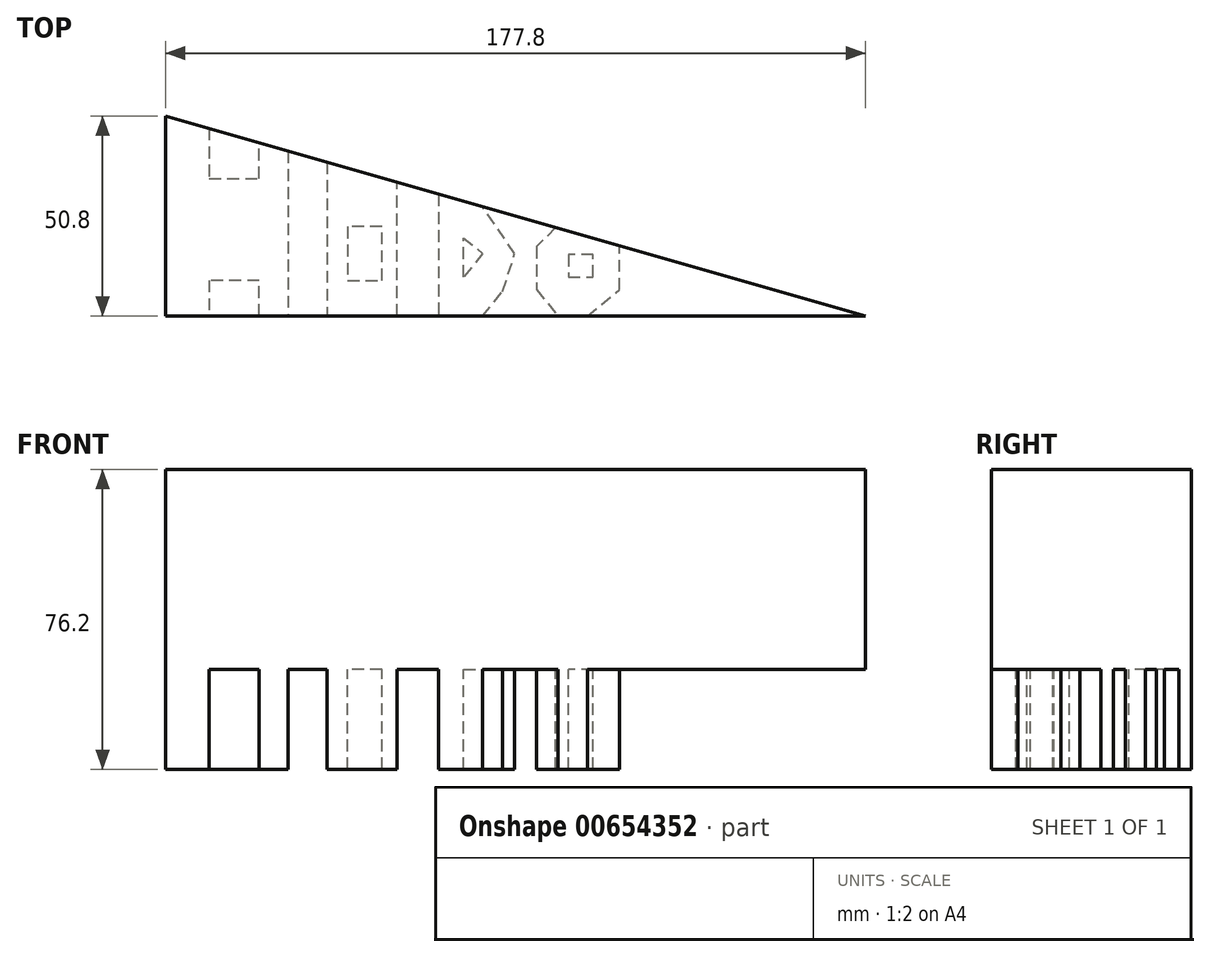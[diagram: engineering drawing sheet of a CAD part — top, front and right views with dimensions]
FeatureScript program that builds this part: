
annotation { "Feature Type Name" : "Feature", "Feature Type Description" : "" }
export const myFeature = defineFeature(function(context is Context, id is Id, definition is map)
    precondition{}
    {
        {
            var Q0;
            Q0=qCreatedBy(makeId("Top.planeOp"),FACE);
            var sketch = newSketch(context, id + "F0", { "sketchPlane" : qUnion([Q0])});
            skLineSegment(sketch, "E0", {"start": v(0, 0) * mm, "end": v(177.8, 0) * mm});
            skLineSegment(sketch, "E1", {"start": v(0, 0) * mm, "end": v(0, 50.8) * mm});
            skLineSegment(sketch, "E2", {"start": v(0, 50.8) * mm, "end": v(177.8, 0) * mm});
            skSolve(sketch);
        }
        {
            var Q0;
            Q0 = qSketchRegion(id + "F0", true);
            extrude(context, id + "F1", {"entities" : qUnion([Q0]), "depth" : 50.8 * mm, "offsetDistance" : 25.4 * mm});
        }
        {
            var Q0;
            Q0=makeQuery(id+"F1.opExtrude","CAP_FACE",FACE,{"disambiguationData":[OSD([sQuery(id+"F0.wireOp",EDGE,"E0"),sQuery(id+"F0.wireOp",EDGE,"E1"),sQuery(id+"F0.wireOp",EDGE,"E2")])],"isStart":false});
            var sketch = newSketch(context, id + "F2", { "sketchPlane" : qUnion([Q0])});
            skLineSegment(sketch, "E3", {"start": v(11.06, 47.64) * mm, "end": v(11.06, 34.94) * mm});
            skLineSegment(sketch, "E4", {"start": v(11.06, 34.94) * mm, "end": v(23.76, 34.94) * mm});
            skLineSegment(sketch, "E5", {"start": v(23.76, 34.94) * mm, "end": v(23.76, 44.01) * mm});
            skLineSegment(sketch, "E6", {"start": v(23.76, 44.01) * mm, "end": v(31.1, 41.92) * mm});
            skLineSegment(sketch, "E7", {"start": v(31.1, 41.92) * mm, "end": v(31.1, 0) * mm});
            skLineSegment(sketch, "E8", {"start": v(31.1, 0) * mm, "end": v(23.76, 0) * mm});
            skLineSegment(sketch, "E9", {"start": v(23.76, 0) * mm, "end": v(23.76, 9.07) * mm});
            skLineSegment(sketch, "E10", {"start": v(23.76, 9.07) * mm, "end": v(11.06, 9.07) * mm});
            skLineSegment(sketch, "E11", {"start": v(11.06, 9.07) * mm, "end": v(11.06, 0) * mm});
            skLineSegment(sketch, "E12", {"start": v(40.97, 39.1) * mm, "end": v(40.97, 0) * mm});
            skLineSegment(sketch, "E13", {"start": v(40.97, 0) * mm, "end": v(58.75, 0) * mm});
            skLineSegment(sketch, "E14", {"start": v(58.75, 0) * mm, "end": v(58.75, 34.01) * mm});
            skLineSegment(sketch, "E15", {"start": v(58.75, 34.01) * mm, "end": v(40.97, 39.1) * mm});
            skLineSegment(sketch, "E16", {"start": v(46.25, 22.72) * mm, "end": v(46.25, 9.07) * mm});
            skLineSegment(sketch, "E17", {"start": v(46.25, 9.07) * mm, "end": v(54.98, 9.07) * mm});
            skLineSegment(sketch, "E18", {"start": v(54.98, 9.07) * mm, "end": v(54.98, 22.72) * mm});
            skLineSegment(sketch, "E19", {"start": v(54.98, 22.72) * mm, "end": v(46.25, 22.72) * mm});
            skLineSegment(sketch, "E20", {"start": v(11.06, 0) * mm, "end": v(0, 0) * mm});
            skLineSegment(sketch, "E21", {"start": v(0, 0) * mm, "end": v(0, 50.8) * mm});
            skLineSegment(sketch, "E22", {"start": v(0, 50.8) * mm, "end": v(11.06, 47.64) * mm});
            skLineSegment(sketch, "E23", {"start": v(69.33, 31) * mm, "end": v(69.33, 0) * mm});
            skLineSegment(sketch, "E24", {"start": v(69.33, 0) * mm, "end": v(80.57, 0) * mm});
            skLineSegment(sketch, "E25", {"start": v(80.57, 0) * mm, "end": v(85.65, 6.27) * mm});
            skLineSegment(sketch, "E26", {"start": v(85.65, 6.27) * mm, "end": v(88.7, 15.81) * mm});
            skLineSegment(sketch, "E27", {"start": v(88.7, 15.81) * mm, "end": v(80.57, 27.78) * mm});
            skLineSegment(sketch, "E28", {"start": v(80.57, 27.78) * mm, "end": v(69.33, 31) * mm});
            skLineSegment(sketch, "E29", {"start": v(75.7, 15.5) * mm, "end": v(75.7, 19.87) * mm});
            skPoint(sketch, "E29.startSnap0", {"position": v(69.33, 15.5) * mm});
            skLineSegment(sketch, "E30", {"start": v(75.7, 19.87) * mm, "end": v(80.57, 15.92) * mm});
            skLineSegment(sketch, "E31", {"start": v(80.57, 15.92) * mm, "end": v(75.7, 9.9) * mm});
            skLineSegment(sketch, "E32", {"start": v(75.7, 9.9) * mm, "end": v(75.7, 19.87) * mm});
            skPoint(sketch, "E33.endSnap0", {"position": v(75.7, 17.68) * mm});
            skLineSegment(sketch, "E34", {"start": v(99.1, 22.48) * mm, "end": v(94.18, 17.64) * mm});
            skLineSegment(sketch, "E35", {"start": v(94.18, 17.64) * mm, "end": v(94.18, 9.9) * mm});
            skLineSegment(sketch, "E36", {"start": v(94.18, 9.9) * mm, "end": v(94.18, 6.67) * mm});
            skLineSegment(sketch, "E37", {"start": v(94.18, 6.67) * mm, "end": v(99.66, 0) * mm});
            skLineSegment(sketch, "E38", {"start": v(99.66, 0) * mm, "end": v(107.18, 0) * mm});
            skLineSegment(sketch, "E39", {"start": v(107.18, 0) * mm, "end": v(115.3, 6.67) * mm});
            skLineSegment(sketch, "E40", {"start": v(115.3, 6.67) * mm, "end": v(115.3, 15.6) * mm});
            skLineSegment(sketch, "E41", {"start": v(115.3, 15.6) * mm, "end": v(115.3, 17.64) * mm});
            skLineSegment(sketch, "E42", {"start": v(115.3, 17.64) * mm, "end": v(99.1, 22.48) * mm});
            skLineSegment(sketch, "E43", {"start": v(102.3, 12.76) * mm, "end": v(102.3, 9.9) * mm});
            skLineSegment(sketch, "E44", {"start": v(102.3, 9.9) * mm, "end": v(108.6, 9.9) * mm});
            skLineSegment(sketch, "E45", {"start": v(108.6, 9.9) * mm, "end": v(108.6, 15.6) * mm});
            skLineSegment(sketch, "E46", {"start": v(108.6, 15.6) * mm, "end": v(102.3, 15.6) * mm});
            skLineSegment(sketch, "E47", {"start": v(102.3, 15.6) * mm, "end": v(102.3, 12.76) * mm});
            skLineSegment(sketch, "E48", {"start": v(127.83, 14.28) * mm, "end": v(127.83, 0) * mm});
            skLineSegment(sketch, "E49", {"start": v(127.83, 0) * mm, "end": v(133.99, 0) * mm});
            skLineSegment(sketch, "E50", {"start": v(133.99, 0) * mm, "end": v(136.02, 5.86) * mm});
            skSolve(sketch);
        }
        {
            var Q0;
            Q0 = qSketchRegion(id + "F2", true);
            extrude(context, id + "F3", {"entities" : qUnion([Q0]), "operationType" : NewBodyOperationType.ADD, "oppositeDirection" : true, "depth" : 76.2 * mm, "offsetDistance" : 25.4 * mm});
        }
    });
